# Revit family: WST-750-5C_SP
name_source: partatom
category: Specialty Equipment
revit_build: Autodesk Revit 2016 (Build: 20150220_1215(x64)
units: mm (PartAtom-declared; Revit-internal decimal feet)

## family parameters
Always vertical = Yes
Cut with Voids When Loaded = No
Part Type = Normal
Room Calculation Point = No
Round Connector Dimension = Use Diameter
Shared = No
Work Plane-Based = No

## types (1)
- WST 750-5C
    A Radio_deposito = 480 mm  [stored 1.5748 ft]
    Agua caliente útil Tª salida 40ºC = 1250 l
    Agua caliente útil Tª salida 45 ºC = 1071 l
    Autor = 6d ingenieros
    Caudal agua intercambiador = 5530 l/h
    Caudal máximo entrada agua fría = 75 l/min
    Clase de eficiencia energética de caldeo = C
    Conexión agua caliente = R1 1/4"
    Conexión agua fría = R1 1/2"
    Conexión recirculación = R3/4"
    Contenido = 750 l
    D Altura tanque = 1920 mm  [stored 6.29921 ft]
    Description = Interacumulador de agua caliente sanitaria de 750 litros de capacidad, modelo WST 750-5C
    E = 144 mm  [stored 0.472441 ft]
    F = 314 mm  [stored 1.03018 ft]
    G = 1004 mm  [stored 3.29396 ft]
    H = 1114 mm  [stored 3.65486 ft]
    I = 1698 mm  [stored 5.57087 ft]
    J = 2450 mm  [stored 8.03806 ft]
    Manufacturer = BOSCH
    Model = WST 750-5C
    Peso en vacío = 241 kg
    PlasticArea = Bosch_160-160-160
    Potencia continua (80ºC imp./45ºC salida ACS/10ºC Suministro) = 103,6 kW
    Potencia máxima de calentamiento = 103,6 kW
    Presión de prueba máxima del agua caliente = 10 bar
    Presión de servicio máxima del agua potable = 10 bar
    Presión máxima intercambiador = 16
    Presión nominal máxima = 7,8 bar
    Pérdida presión intercambiador (agua) = 350 mbar
    Radio Impulsión acumulador = 16 mm
    Radio circulación = 10 mm  [stored 0.0328084 ft]
    Radio entrada agua fría = 19 mm  [stored 0.062336 ft]
    Radio puerta = 490 mm  [stored 1.60761 ft]
    Radio retorno acumulador = 16 mm
    Radio salida agua caliente = 16 mm
    Radio sonda = 10 mm  [stored 0.0328084 ft]
    Temperatura máxima intercambiador = 160 ºC
    Tiempo calentamiento con petencia nominal = 42 min
    Tª máxima agua caliente = 95 ºC
    URL = www.bosch-thermotechnology.com/es/es/comercial-e-industrial/ocs/stora-w-st--5-742030-p
    Versión = 1.0

note: [stored X ft] marks values corroborated as IEEE doubles in the binary element streams (Revit-internal decimal feet)

## geometry (parser evidence)
native form markers: Sweep x2
no freeform markers — native parametric forms only
